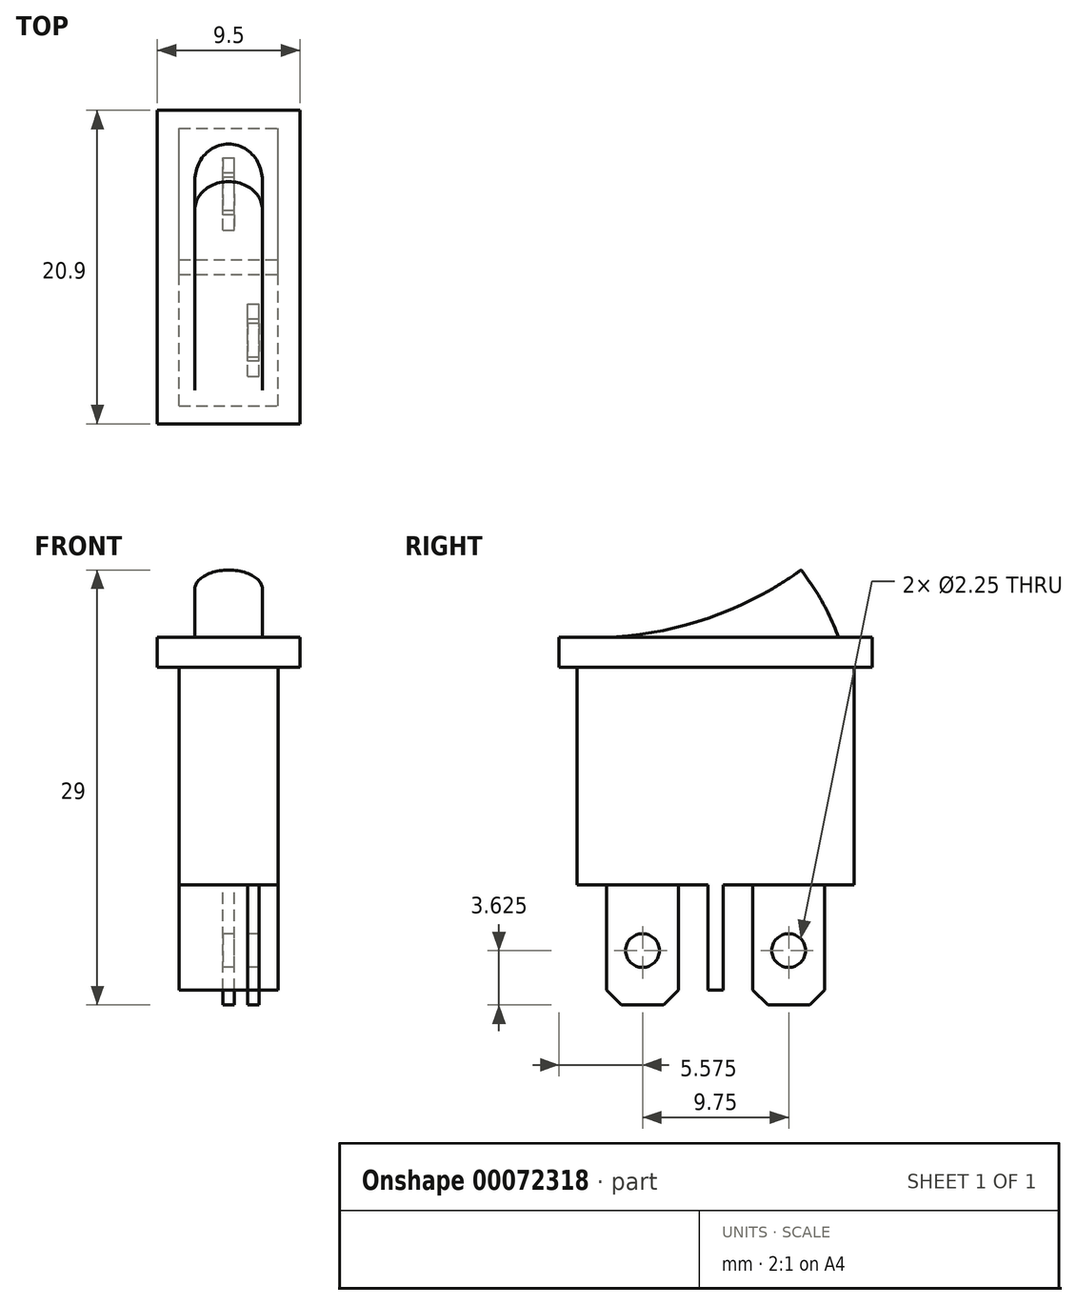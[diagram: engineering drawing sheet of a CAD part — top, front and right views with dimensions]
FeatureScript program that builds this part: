
annotation { "Feature Type Name" : "Feature", "Feature Type Description" : "" }
export const myFeature = defineFeature(function(context is Context, id is Id, definition is map)
    precondition{}
    {
        {
            var Q0;
            Q0=qCreatedBy(makeId("Top.planeOp"),FACE);
            var sketch = newSketch(context, id + "F0", { "sketchPlane" : qUnion([Q0])});
            skLineSegment(sketch, "E0.bottom", {"start": v(-4.75, 10.45) * mm, "end": v(4.75, 10.45) * mm});
            skLineSegment(sketch, "E0.top", {"start": v(-4.75, -10.45) * mm, "end": v(4.75, -10.45) * mm});
            skLineSegment(sketch, "E0.left", {"start": v(-4.75, 10.45) * mm, "end": v(-4.75, -10.45) * mm});
            skLineSegment(sketch, "E0.right", {"start": v(4.75, 10.45) * mm, "end": v(4.75, -10.45) * mm});
            skPoint(sketch, "E1", {"position": v(0, 10.45) * mm});
            skPoint(sketch, "E2", {"position": v(-4.75, 0) * mm});
            skSolve(sketch);
        }
        {
            var Q0;
            Q0 = qSketchRegion(id + "F0", true);
            extrude(context, id + "F1", {"entities" : qUnion([Q0]), "depth" : 2 * mm});
        }
        {
            var Q0;
            Q0=makeQuery(id+"F1.opExtrude","CAP_FACE",FACE,{"disambiguationData":[OSD([sQuery(id+"F0.wireOp",EDGE,"E0.bottom"),sQuery(id+"F0.wireOp",EDGE,"E0.top"),sQuery(id+"F0.wireOp",EDGE,"E0.left"),sQuery(id+"F0.wireOp",EDGE,"E0.right")])],"isStart":true});
            var sketch = newSketch(context, id + "F2", { "sketchPlane" : qUnion([Q0])});
            skLineSegment(sketch, "E3.bottom", {"start": v(-3.3, 9.25) * mm, "end": v(3.3, 9.25) * mm});
            skLineSegment(sketch, "E3.top", {"start": v(-3.3, -9.25) * mm, "end": v(3.3, -9.25) * mm});
            skLineSegment(sketch, "E3.left", {"start": v(-3.3, 9.25) * mm, "end": v(-3.3, -9.25) * mm});
            skLineSegment(sketch, "E3.right", {"start": v(3.3, 9.25) * mm, "end": v(3.3, -9.25) * mm});
            skPoint(sketch, "E4", {"position": v(0, 9.25) * mm});
            skPoint(sketch, "E5", {"position": v(-3.3, 0) * mm});
            skSolve(sketch);
        }
        {
            var Q0;
            Q0 = qSketchRegion(id + "F2", true);
            extrude(context, id + "F3", {"entities" : qUnion([Q0]), "operationType" : NewBodyOperationType.ADD, "depth" : 14.5 * mm});
        }
        {
            var Q0;
            Q0=makeQuery(id+"F3.opExtrude","CAP_FACE",FACE,{"disambiguationData":[OSD([sQuery(id+"F2.wireOp",EDGE,"E3.bottom"),sQuery(id+"F2.wireOp",EDGE,"E3.top"),sQuery(id+"F2.wireOp",EDGE,"E3.left"),sQuery(id+"F2.wireOp",EDGE,"E3.right")])],"isStart":false});
            var sketch = newSketch(context, id + "F4", { "sketchPlane" : qUnion([Q0])});
            skLineSegment(sketch, "E6.bottom", {"start": v(-3.3, 0.5) * mm, "end": v(3.3, 0.5) * mm});
            skLineSegment(sketch, "E6.top", {"start": v(-3.3, -0.5) * mm, "end": v(3.3, -0.5) * mm});
            skLineSegment(sketch, "E6.left", {"start": v(-3.3, 0.5) * mm, "end": v(-3.3, -0.5) * mm});
            skLineSegment(sketch, "E6.right", {"start": v(3.3, 0.5) * mm, "end": v(3.3, -0.5) * mm});
            skPoint(sketch, "E7", {"position": v(0, 0.5) * mm});
            skPoint(sketch, "E8", {"position": v(3.3, 0) * mm});
            skLineSegment(sketch, "E9.bottom", {"start": v(1.28, 7.27) * mm, "end": v(2.03, 7.27) * mm});
            skLineSegment(sketch, "E9.top", {"start": v(1.28, 2.47) * mm, "end": v(2.03, 2.47) * mm});
            skLineSegment(sketch, "E9.left", {"start": v(1.28, 7.27) * mm, "end": v(1.28, 2.47) * mm});
            skLineSegment(sketch, "E9.right", {"start": v(2.03, 7.27) * mm, "end": v(2.03, 2.47) * mm});
            skLineSegment(sketch, "E10.bottom", {"start": v(-0.38, -2.47) * mm, "end": v(0.38, -2.47) * mm});
            skLineSegment(sketch, "E10.top", {"start": v(-0.38, -7.28) * mm, "end": v(0.38, -7.28) * mm});
            skLineSegment(sketch, "E10.left", {"start": v(-0.37, -2.47) * mm, "end": v(-0.38, -7.28) * mm});
            skLineSegment(sketch, "E10.right", {"start": v(0.38, -2.47) * mm, "end": v(0.37, -7.28) * mm});
            skPoint(sketch, "E11", {"position": v(0, -2.47) * mm});
            skLineSegment(sketch, "E12", {"start": v(3.3, 0.5) * mm, "end": v(3.3, 9.25) * mm});
            skLineSegment(sketch, "E13", {"start": v(3.3, -0.5) * mm, "end": v(3.3, -9.25) * mm});
            skPoint(sketch, "E14", {"position": v(0.37, -4.88) * mm});
            skPoint(sketch, "E15", {"position": v(2.03, 4.88) * mm});
            skPoint(sketch, "E16", {"position": v(3.3, 4.87) * mm});
            skPoint(sketch, "E17", {"position": v(3.3, -4.88) * mm});
            skLineSegment(sketch, "E18", {"start": v(0, 0.5) * mm, "end": v(3.3, 0.5) * mm});
            skPoint(sketch, "E19", {"position": v(1.65, 2.47) * mm});
            skPoint(sketch, "E20", {"position": v(1.65, 0.5) * mm});
            skSolve(sketch);
        }
        {
            var Q0;
            Q0 = qSketchRegion(id + "F4", true);
            extrude(context, id + "F5", {"entities" : qUnion([Q0]), "operationType" : NewBodyOperationType.ADD, "depth" : 7 * mm});
        }
        {
            var Q0;
            Q0=makeQuery(id+"F5.opExtrude","CAP_FACE",FACE,{"disambiguationData":[OSD([sQuery(id+"F4.wireOp",EDGE,"E9.bottom"),sQuery(id+"F4.wireOp",EDGE,"E9.top"),sQuery(id+"F4.wireOp",EDGE,"E9.left"),sQuery(id+"F4.wireOp",EDGE,"E9.right")])],"isStart":false});
            var Q1;
            Q1=makeQuery(id+"F5.opExtrude","CAP_FACE",FACE,{"disambiguationData":[OSD([sQuery(id+"F4.wireOp",EDGE,"E10.bottom"),sQuery(id+"F4.wireOp",EDGE,"E10.top"),sQuery(id+"F4.wireOp",EDGE,"E10.left"),sQuery(id+"F4.wireOp",EDGE,"E10.right")])],"isStart":false});
            extrude(context, id + "F6", {"entities" : qUnion([Q0, Q1]), "operationType" : NewBodyOperationType.ADD, "depth" : 1 * mm});
        }
        {
            var Q0;
            {var subQ0=sQuery(id+"F4.wireOp",EDGE,"E10.left");Q0=makeQuery(id+"F6.boolean.opBoolean","MERGE",FACE,{"derivedFrom":[makeQuery(id+"F5.opExtrude","SWEPT_FACE",FACE,{"disambiguationData":[OSD([subQ0])]}),makeQuery(id+"F6.opExtrude","SWEPT_FACE",FACE,{"disambiguationData":[OSD([subQ0])]})]});}
            var sketch = newSketch(context, id + "F7", { "sketchPlane" : qUnion([Q0])});
            skPoint(sketch, "E21.0", {"position": v(-0.5, -21.5) * mm});
            skLineSegment(sketch, "E22", {"start": v(-7.28, -21.5) * mm, "end": v(-6.27, -22.5) * mm});
            skLineSegment(sketch, "E23", {"start": v(-6.27, -22.5) * mm, "end": v(-7.28, -22.5) * mm});
            skLineSegment(sketch, "E24", {"start": v(-7.28, -22.5) * mm, "end": v(-7.28, -21.5) * mm});
            skLineSegment(sketch, "E25", {"start": v(-2.47, -21.5) * mm, "end": v(-3.47, -22.5) * mm});
            skLineSegment(sketch, "E26", {"start": v(-3.48, -22.5) * mm, "end": v(-2.47, -22.5) * mm});
            skLineSegment(sketch, "E27", {"start": v(-2.47, -22.5) * mm, "end": v(-2.47, -21.5) * mm});
            skLineSegment(sketch, "E28.0", {"start": v(2.47, -22.5) * mm, "end": v(2.47, -14.5) * mm});
            skLineSegment(sketch, "E29.0", {"start": v(7.27, -22.5) * mm, "end": v(7.27, -14.5) * mm});
            skLineSegment(sketch, "E30", {"start": v(2.47, -21.5) * mm, "end": v(3.48, -22.5) * mm});
            skLineSegment(sketch, "E31", {"start": v(3.48, -22.5) * mm, "end": v(2.47, -22.5) * mm});
            skLineSegment(sketch, "E32", {"start": v(7.27, -22.5) * mm, "end": v(6.27, -22.5) * mm});
            skLineSegment(sketch, "E33", {"start": v(6.27, -22.5) * mm, "end": v(7.28, -21.5) * mm});
            skLineSegment(sketch, "E34", {"start": v(7.27, -21.5) * mm, "end": v(7.27, -22.5) * mm});
            skCircle(sketch, "E35", {"center": v(-4.88, -18.88) * mm, "radius": 1.13 * mm});
            skLineSegment(sketch, "E36", {"start": v(2.47, -14.5) * mm, "end": v(7.27, -14.5) * mm});
            skLineSegment(sketch, "E37", {"start": v(-7.28, -14.5) * mm, "end": v(-2.47, -14.5) * mm});
            skPoint(sketch, "E38", {"position": v(-4.88, -14.5) * mm});
            skPoint(sketch, "E39", {"position": v(4.87, -14.5) * mm});
            skCircle(sketch, "E40", {"center": v(4.87, -18.88) * mm, "radius": 1.13 * mm});
            skSolve(sketch);
        }
        {
            var Q0;
            Q0 = qSketchRegion(id + "F7", true);
            extrude(context, id + "F8", {"entities" : qUnion([Q0]), "operationType" : NewBodyOperationType.REMOVE, "endBound" : BoundingType.THROUGH_ALL, "oppositeDirection" : true, "depth" : 25 * mm});
        }
        {
            var Q0;
            Q0=qCreatedBy(makeId("Right.planeOp"),FACE);
            var sketch = newSketch(context, id + "F9", { "sketchPlane" : qUnion([Q0])});
            skPoint(sketch, "E41", {"position": v(0, -1) * mm});
            skLineSegment(sketch, "E42.0", {"start": v(10.45, 2) * mm, "end": v(-10.45, 2) * mm});
            skPoint(sketch, "E43", {"position": v(8.2, 2) * mm});
            skPoint(sketch, "E44", {"position": v(0, 2) * mm});
            skLineSegment(sketch, "E45", {"start": v(8.2, 2) * mm, "end": v(-8.21, -4) * mm, "construction": true});
            skArc(sketch, "E46", {"start": v(8.2, 2) * mm, "mid": v(7.13, 4.35) * mm, "end": v(5.7, 6.5) * mm});
            skLineSegment(sketch, "E47", {"start": v(8.2, 2) * mm, "end": v(0, 2) * mm});
            skLineSegment(sketch, "E48", {"start": v(0, 2) * mm, "end": v(-8.2, 2) * mm});
            skArc(sketch, "E49", {"start": v(5.7, 6.5) * mm, "mid": v(-0.9, 3.15) * mm, "end": v(-8.2, 2) * mm});
            skSolve(sketch);
        }
        {
            var Q0;
            Q0 = qSketchRegion(id + "F9", true);
            extrude(context, id + "F10", {"entities" : qUnion([Q0]), "operationType" : NewBodyOperationType.ADD, "endBound" : BoundingType.SYMMETRIC, "depth" : 4.5 * mm});
        }
        {
            var Q0;
            Q0=makeQuery(id+"F10.opExtrude","CAP_EDGE",EDGE,{"disambiguationData":[OSD([sQuery(id+"F9.wireOp",EDGE,"E46")])],"isStart":false});
            var Q1;
            Q1=makeQuery(id+"F10.opExtrude","CAP_EDGE",EDGE,{"disambiguationData":[OSD([sQuery(id+"F9.wireOp",EDGE,"E46")])],"isStart":true});
            fillet(context, id + "F11", {"entities" : qUnion([Q0, Q1]), "radius" : 2.25 * mm, "tangentPropagation" : true, "allowEdgeOverflow" : false});
        }
    });
